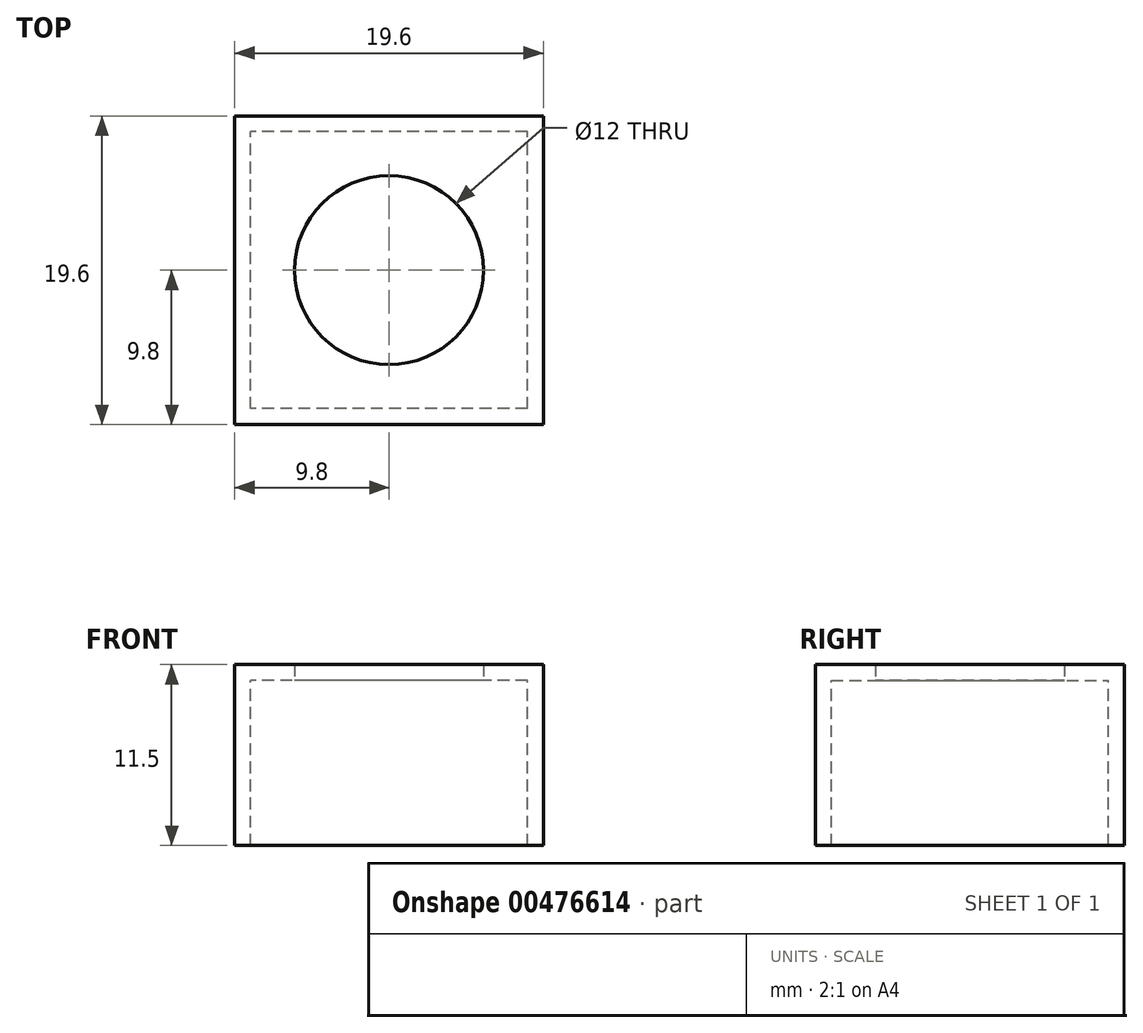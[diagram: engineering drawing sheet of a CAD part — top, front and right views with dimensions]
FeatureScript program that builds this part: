
annotation { "Feature Type Name" : "Feature", "Feature Type Description" : "" }
export const myFeature = defineFeature(function(context is Context, id is Id, definition is map)
    precondition{}
    {
        {
            var Q0;
            Q0=qCreatedBy(makeId("Top.planeOp"),FACE);
            var sketch = newSketch(context, id + "F0", { "sketchPlane" : qUnion([Q0])});
            skLineSegment(sketch, "E0.bottom", {"start": v(9.8, 9.8) * mm, "end": v(-9.8, 9.8) * mm});
            skLineSegment(sketch, "E0.top", {"start": v(9.8, -9.8) * mm, "end": v(-9.8, -9.8) * mm});
            skLineSegment(sketch, "E0.left", {"start": v(9.8, 9.8) * mm, "end": v(9.8, -9.8) * mm});
            skLineSegment(sketch, "E0.right", {"start": v(-9.8, 9.8) * mm, "end": v(-9.8, -9.8) * mm});
            skPoint(sketch, "E0.middle", {"position": v(0, 0) * mm});
            skCircle(sketch, "E1", {"center": v(0, 0) * mm, "radius": 6 * mm});
            skSolve(sketch);
        }
        {
            var Q0;
            Q0 = qSketchRegion(id + "F0", true);
            extrude(context, id + "F1", {"entities" : qUnion([Q0]), "offsetDistance" : 25 * mm, "depth" : 1 * mm});
        }
        {
            var Q0;
            Q0=makeQuery(id+"F1.opExtrude","CAP_FACE",FACE,{"disambiguationData":[OSD([sQuery(id+"F0.wireOp",EDGE,"E0.bottom"),sQuery(id+"F0.wireOp",EDGE,"E0.top"),sQuery(id+"F0.wireOp",EDGE,"E0.left"),sQuery(id+"F0.wireOp",EDGE,"E0.right"),sQuery(id+"F0.wireOp",EDGE,"E1")])],"isStart":true});
            var sketch = newSketch(context, id + "F2", { "sketchPlane" : qUnion([Q0])});
            skLineSegment(sketch, "E2.bottom", {"start": v(9.8, 9.8) * mm, "end": v(-9.8, 9.8) * mm});
            skLineSegment(sketch, "E2.top", {"start": v(9.8, -9.8) * mm, "end": v(-9.8, -9.8) * mm});
            skLineSegment(sketch, "E2.left", {"start": v(9.8, 9.8) * mm, "end": v(9.8, -9.8) * mm});
            skLineSegment(sketch, "E2.right", {"start": v(-9.8, 9.8) * mm, "end": v(-9.8, -9.8) * mm});
            skPoint(sketch, "E2.middle", {"position": v(0, 0) * mm});
            skLineSegment(sketch, "E3.bottom", {"start": v(8.8, 8.8) * mm, "end": v(-8.8, 8.8) * mm});
            skLineSegment(sketch, "E3.top", {"start": v(8.8, -8.8) * mm, "end": v(-8.8, -8.8) * mm});
            skLineSegment(sketch, "E3.left", {"start": v(8.8, 8.8) * mm, "end": v(8.8, -8.8) * mm});
            skLineSegment(sketch, "E3.right", {"start": v(-8.8, 8.8) * mm, "end": v(-8.8, -8.8) * mm});
            skSolve(sketch);
        }
        {
            var Q0;
            Q0 = qSketchRegion(id + "F2", true);
            extrude(context, id + "F3", {"entities" : qUnion([Q0]), "operationType" : NewBodyOperationType.ADD, "offsetDistance" : 25 * mm, "depth" : 10.5 * mm});
        }
    });
